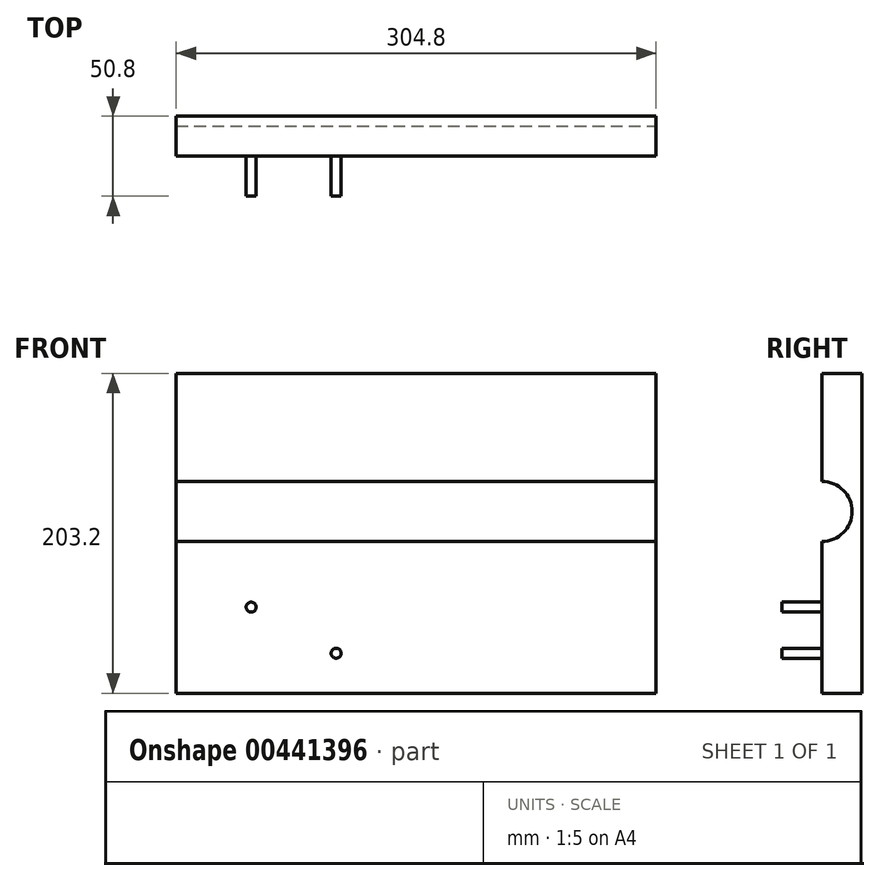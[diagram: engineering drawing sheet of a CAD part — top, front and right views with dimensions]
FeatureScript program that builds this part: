
annotation { "Feature Type Name" : "Feature", "Feature Type Description" : "" }
export const myFeature = defineFeature(function(context is Context, id is Id, definition is map)
    precondition{}
    {
        {
            var Q0;
            Q0=qCreatedBy(makeId("Front.planeOp"),FACE);
            var sketch = newSketch(context, id + "F0", { "sketchPlane" : qUnion([Q0])});
            skLineSegment(sketch, "E0.bottom", {"start": v(149.35, 104.57) * mm, "end": v(-155.45, 104.57) * mm});
            skLineSegment(sketch, "E0.top", {"start": v(149.35, -98.63) * mm, "end": v(-155.45, -98.63) * mm});
            skLineSegment(sketch, "E0.left", {"start": v(149.35, 104.57) * mm, "end": v(149.35, -98.63) * mm});
            skLineSegment(sketch, "E0.right", {"start": v(-155.45, 104.57) * mm, "end": v(-155.45, -98.63) * mm});
            skSolve(sketch);
        }
        {
            var Q0;
            Q0=makeQuery(id+"F0.imprint","IMPRINT",FACE,{"disambiguationData":[TD([[makeQuery(id+"F0.imprint","IMPRINT",EDGE,{"derivedFrom":sQuery(id+"F0.wireOp",EDGE,"E0.bottom")}),1.0]])]});
            extrude(context, id + "F1", {"entities" : qUnion([Q0]), "depth" : 25.4 * mm});
        }
        {
            var Q0;
            Q0=makeQuery(id+"F1.opExtrude","CAP_FACE",FACE,{"disambiguationData":[OSD([sQuery(id+"F0.wireOp",EDGE,"E0.bottom"),sQuery(id+"F0.wireOp",EDGE,"E0.top"),sQuery(id+"F0.wireOp",EDGE,"E0.left"),sQuery(id+"F0.wireOp",EDGE,"E0.right")])],"isStart":false});
            var sketch = newSketch(context, id + "F2", { "sketchPlane" : qUnion([Q0])});
            skCircle(sketch, "E1", {"center": v(-53.85, -73.23) * mm, "radius": 3.18 * mm});
            skCircle(sketch, "E2", {"center": v(-107.8, -43.93) * mm, "radius": 3.18 * mm});
            skSolve(sketch);
        }
        {
            var Q0;
            Q0 = qSketchRegion(id + "F2", true);
            extrude(context, id + "F3", {"entities" : qUnion([Q0]), "operationType" : NewBodyOperationType.ADD, "depth" : 25.4 * mm});
        }
        {
            var Q0;
            Q0=makeQuery(id+"F1.opExtrude","CAP_FACE",FACE,{"disambiguationData":[OSD([sQuery(id+"F0.wireOp",EDGE,"E0.bottom"),sQuery(id+"F0.wireOp",EDGE,"E0.top"),sQuery(id+"F0.wireOp",EDGE,"E0.left"),sQuery(id+"F0.wireOp",EDGE,"E0.right")])],"isStart":false});
            var sketch = newSketch(context, id + "F4", { "sketchPlane" : qUnion([Q0])});
            skPoint(sketch, "E3", {"position": v(-76.88, -2.22) * mm});
            skLineSegment(sketch, "E4", {"start": v(-155.45, 16.83) * mm, "end": v(149.35, 16.83) * mm});
            skLineSegment(sketch, "E5", {"start": v(-76.88, -2.22) * mm, "end": v(-155.45, -2.22) * mm});
            skLineSegment(sketch, "E6", {"start": v(-155.45, -2.22) * mm, "end": v(-155.45, 16.83) * mm});
            skLineSegment(sketch, "E7", {"start": v(-76.88, -2.22) * mm, "end": v(149.35, -2.22) * mm});
            skLineSegment(sketch, "E8", {"start": v(149.35, -2.22) * mm, "end": v(149.35, 16.83) * mm});
            skSolve(sketch);
        }
        {
            var Q0;
            Q0=makeQuery(id+"F4.imprint","IMPRINT",FACE,{"disambiguationData":[TD([[makeQuery(id+"F4.imprint","IMPRINT",EDGE,{"derivedFrom":sQuery(id+"F4.wireOp",EDGE,"E4")}),-1.0]])]});
            var Q1;
            Q1=sQuery(id+"F4.wireOp",EDGE,"E4");
            revolve(context, id + "F5", {"operationType" : NewBodyOperationType.REMOVE, "entities" : qUnion([Q0]), "axis" : qUnion([Q1]), "revolveType" : RevolveType.FULL, "oppositeDirection" : true});
        }
    });
